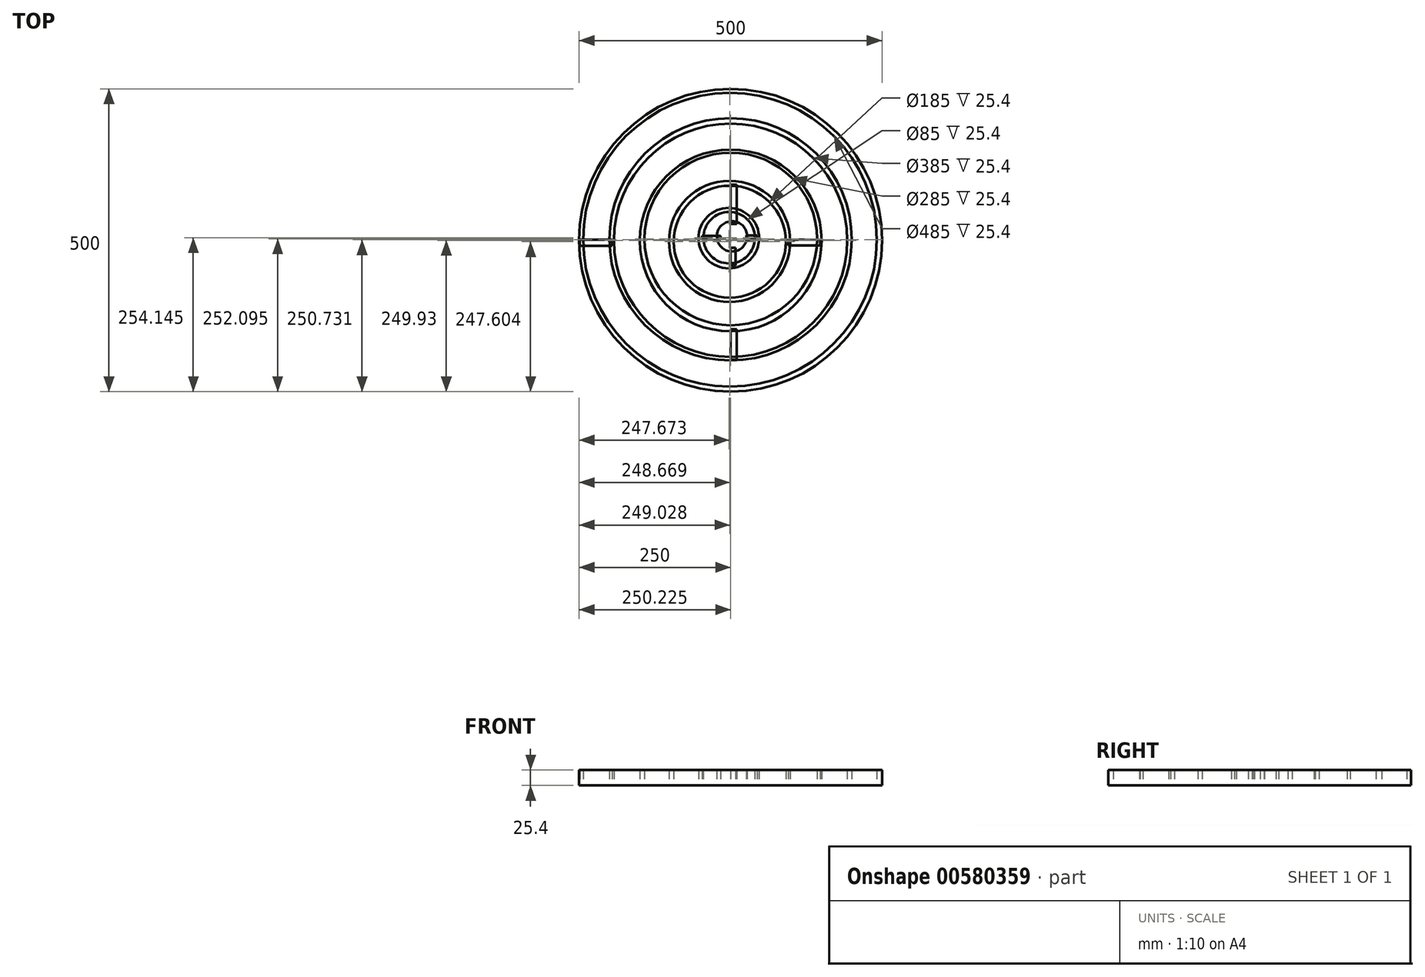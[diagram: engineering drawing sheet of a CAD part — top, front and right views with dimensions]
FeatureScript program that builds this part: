
annotation { "Feature Type Name" : "Feature", "Feature Type Description" : "" }
export const myFeature = defineFeature(function(context is Context, id is Id, definition is map)
    precondition{}
    {
        {
            var Q0;
            Q0=qCreatedBy(makeId("Top.planeOp"),FACE);
            var sketch = newSketch(context, id + "F0", { "sketchPlane" : qUnion([Q0])});
            skCircle(sketch, "E0", {"center": v(-0.23, -0.87) * mm, "radius": 250 * mm});
            skCircle(sketch, "E1", {"center": v(-1.2, -0.14) * mm, "radius": 242.5 * mm});
            skSolve(sketch);
        }
        {
            var Q0;
            Q0=qCreatedBy(makeId("Top.planeOp"),FACE);
            var sketch = newSketch(context, id + "F1", { "sketchPlane" : qUnion([Q0])});
            skCircle(sketch, "E2", {"center": v(-0.23, 0.62) * mm, "radius": 200 * mm});
            skCircle(sketch, "E3", {"center": v(-0.23, -0.94) * mm, "radius": 192.5 * mm});
            skSolve(sketch);
        }
        {
            var Q0;
            Q0=qCreatedBy(makeId("Top.planeOp"),FACE);
            var sketch = newSketch(context, id + "F2", { "sketchPlane" : qUnion([Q0])});
            skCircle(sketch, "E4", {"center": v(0, -1.2) * mm, "radius": 150 * mm});
            skCircle(sketch, "E5", {"center": v(0, 1.23) * mm, "radius": 142.5 * mm});
            skSolve(sketch);
        }
        {
            var Q0;
            Q0=qCreatedBy(makeId("Top.planeOp"),FACE);
            var sketch = newSketch(context, id + "F3", { "sketchPlane" : qUnion([Q0])});
            skCircle(sketch, "E6", {"center": v(-1.92, -2.72) * mm, "radius": 100 * mm});
            skCircle(sketch, "E7", {"center": v(-1.56, -3.27) * mm, "radius": 92.5 * mm});
            skSolve(sketch);
        }
        {
            var Q0;
            Q0=qCreatedBy(makeId("Top.planeOp"),FACE);
            var sketch = newSketch(context, id + "F4", { "sketchPlane" : qUnion([Q0])});
            skCircle(sketch, "E8", {"center": v(-3.22, 2.62) * mm, "radius": 50 * mm});
            skCircle(sketch, "E9", {"center": v(-2.56, 3.28) * mm, "radius": 42.5 * mm});
            skSolve(sketch);
        }
        {
            var Q0;
            Q0=qCreatedBy(makeId("Top.planeOp"),FACE);
            var sketch = newSketch(context, id + "F5", { "sketchPlane" : qUnion([Q0])});
            skCircle(sketch, "E10", {"center": v(2.15, 5.57) * mm, "radius": 25 * mm});
            skSolve(sketch);
        }
        {
            var Q0;
            Q0 = qSketchRegion(id + "F0", true);
            extrude(context, id + "F6", {"entities" : qUnion([Q0]), "depth" : 25.4 * mm, "offsetDistance" : 25.4 * mm});
        }
        {
            var Q0;
            Q0 = qSketchRegion(id + "F1", true);
            extrude(context, id + "F7", {"entities" : qUnion([Q0]), "depth" : 25.4 * mm, "offsetDistance" : 25.4 * mm});
        }
        {
            var Q0;
            Q0 = qSketchRegion(id + "F2", true);
            extrude(context, id + "F8", {"entities" : qUnion([Q0]), "depth" : 25.4 * mm, "offsetDistance" : 25.4 * mm});
        }
        {
            var Q0;
            Q0 = qSketchRegion(id + "F3", true);
            extrude(context, id + "F9", {"entities" : qUnion([Q0]), "depth" : 25.4 * mm, "offsetDistance" : 25.4 * mm});
        }
        {
            var Q0;
            Q0 = qSketchRegion(id + "F4", true);
            extrude(context, id + "F10", {"entities" : qUnion([Q0]), "depth" : 25.4 * mm, "offsetDistance" : 25.4 * mm});
        }
        {
            var Q0;
            Q0 = qSketchRegion(id + "F5", true);
            extrude(context, id + "F11", {"entities" : qUnion([Q0]), "depth" : 25.4 * mm, "offsetDistance" : 25.4 * mm});
        }
        {
            var Q0;
            Q0=makeQuery(id+"F0.imprint","IMPRINT",FACE,{"disambiguationData":[TD([[makeQuery(id+"F0.imprint","IMPRINT",EDGE,{"derivedFrom":sQuery(id+"F0.wireOp",EDGE,"E1")}),1.0]])]});
            var sketch = newSketch(context, id + "F12", { "sketchPlane" : qUnion([Q0])});
            skLineSegment(sketch, "E11.bottom", {"start": v(-249.38, 0) * mm, "end": v(-195.96, 0) * mm});
            skLineSegment(sketch, "E11.top", {"start": v(-249.38, -10.4) * mm, "end": v(-195.96, -10.4) * mm});
            skLineSegment(sketch, "E11.left", {"start": v(-249.38, 0) * mm, "end": v(-249.38, -10.4) * mm});
            skLineSegment(sketch, "E11.right", {"start": v(-195.96, 0) * mm, "end": v(-195.96, -10.4) * mm});
            skLineSegment(sketch, "E12.bottom", {"start": v(0, -198.13) * mm, "end": v(10.07, -198.13) * mm});
            skLineSegment(sketch, "E12.top", {"start": v(0, -147.76) * mm, "end": v(10.07, -147.76) * mm});
            skLineSegment(sketch, "E12.left", {"start": v(0, -198.13) * mm, "end": v(0, -147.76) * mm});
            skLineSegment(sketch, "E12.right", {"start": v(10.07, -198.13) * mm, "end": v(10.07, -147.76) * mm});
            skLineSegment(sketch, "E13.bottom", {"start": v(94.77, 0) * mm, "end": v(147.43, 0) * mm});
            skLineSegment(sketch, "E13.top", {"start": v(94.77, -9.64) * mm, "end": v(147.43, -9.64) * mm});
            skLineSegment(sketch, "E13.left", {"start": v(94.77, 0) * mm, "end": v(94.77, -9.64) * mm});
            skLineSegment(sketch, "E13.right", {"start": v(147.43, 0) * mm, "end": v(147.43, -9.64) * mm});
            skLineSegment(sketch, "E14.bottom", {"start": v(0, 49.11) * mm, "end": v(10.07, 49.11) * mm});
            skLineSegment(sketch, "E14.top", {"start": v(0, 91.08) * mm, "end": v(10.07, 91.08) * mm});
            skLineSegment(sketch, "E14.left", {"start": v(0, 49.11) * mm, "end": v(0, 91.08) * mm});
            skLineSegment(sketch, "E14.right", {"start": v(10.07, 49.11) * mm, "end": v(10.07, 91.08) * mm});
            skLineSegment(sketch, "E15.bottom", {"start": v(0, 26.22) * mm, "end": v(10.07, 26.22) * mm});
            skLineSegment(sketch, "E15.left", {"start": v(0, 26.22) * mm, "end": v(0, 49.11) * mm});
            skLineSegment(sketch, "E15.right", {"start": v(10.07, 26.22) * mm, "end": v(10.07, 49.11) * mm});
            skLineSegment(sketch, "E16.bottom", {"start": v(-47.16, 0) * mm, "end": v(-16.64, 0) * mm});
            skLineSegment(sketch, "E16.top", {"start": v(-47.16, 6.38) * mm, "end": v(-16.64, 6.38) * mm});
            skLineSegment(sketch, "E16.left", {"start": v(-47.16, 0) * mm, "end": v(-47.16, 6.38) * mm});
            skLineSegment(sketch, "E16.right", {"start": v(-16.64, 0) * mm, "end": v(-16.64, 6.38) * mm});
            skLineSegment(sketch, "E17.bottom", {"start": v(26.1, 7.14) * mm, "end": v(43.65, 7.14) * mm});
            skLineSegment(sketch, "E17.top", {"start": v(26.1, 0) * mm, "end": v(43.65, 0) * mm});
            skLineSegment(sketch, "E17.left", {"start": v(26.1, 7.14) * mm, "end": v(26.1, 0) * mm});
            skLineSegment(sketch, "E17.right", {"start": v(43.65, 7.14) * mm, "end": v(43.65, 0) * mm});
            skLineSegment(sketch, "E18.bottom", {"start": v(0, -13.46) * mm, "end": v(7.78, -13.46) * mm});
            skLineSegment(sketch, "E18.top", {"start": v(0, -42.46) * mm, "end": v(7.78, -42.46) * mm});
            skLineSegment(sketch, "E18.left", {"start": v(0, -13.46) * mm, "end": v(0, -42.46) * mm});
            skLineSegment(sketch, "E18.right", {"start": v(7.78, -13.46) * mm, "end": v(7.78, -42.46) * mm});
            skSolve(sketch);
        }
        {
            var Q0;
            Q0 = qSketchRegion(id + "F12", true);
            extrude(context, id + "F13", {"entities" : qUnion([Q0]), "depth" : 25.4 * mm, "offsetDistance" : 25.4 * mm});
        }
    });
